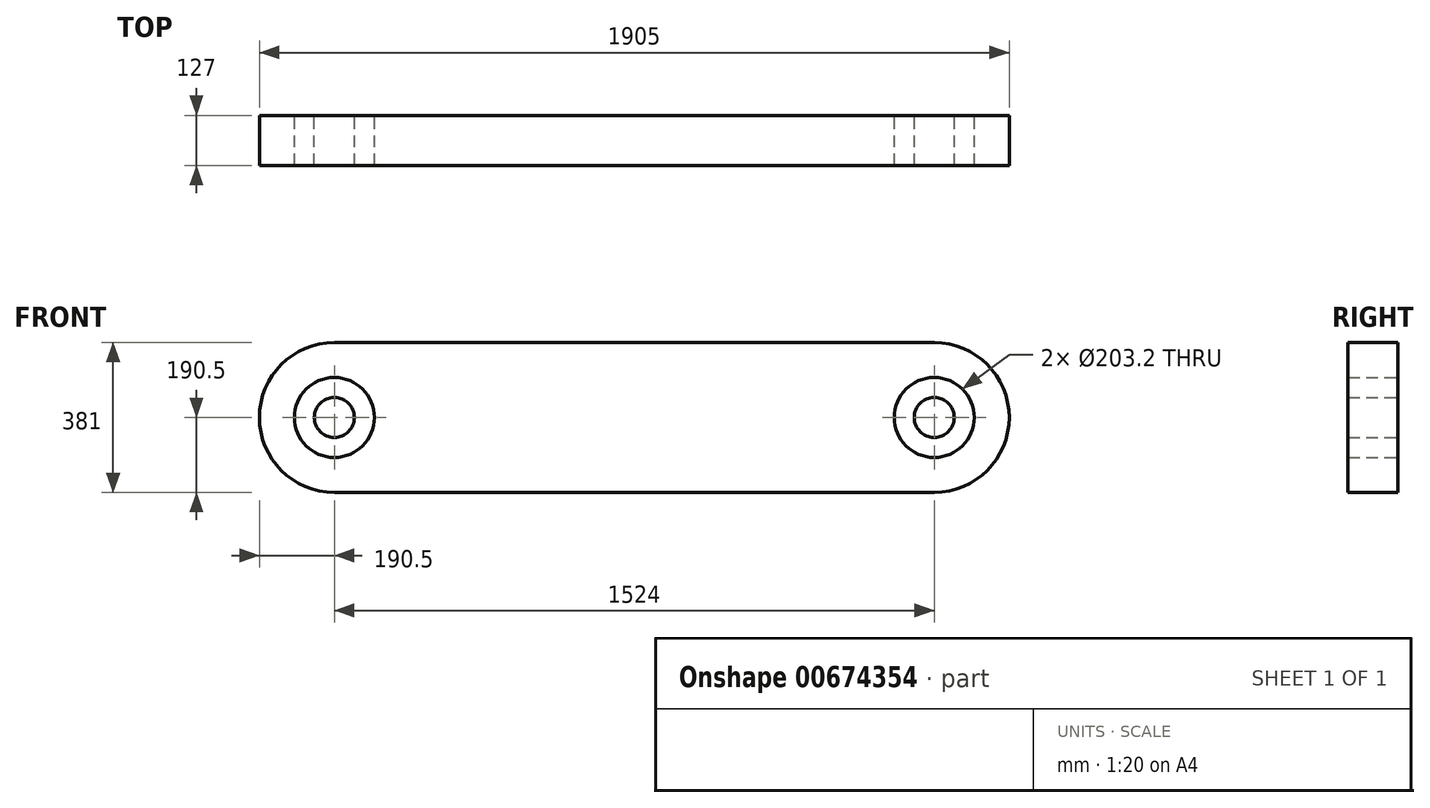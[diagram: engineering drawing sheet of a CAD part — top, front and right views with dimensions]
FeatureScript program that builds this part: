
annotation { "Feature Type Name" : "Feature", "Feature Type Description" : "" }
export const myFeature = defineFeature(function(context is Context, id is Id, definition is map)
    precondition{}
    {
        {
            var Q0;
            Q0=qCreatedBy(makeId("Front.planeOp"),FACE);
            var sketch = newSketch(context, id + "F0", { "sketchPlane" : qUnion([Q0])});
            skLineSegment(sketch, "E0.bottom", {"start": v(0, 0) * mm, "end": v(1524, 0) * mm});
            skLineSegment(sketch, "E0.top", {"start": v(0, 381) * mm, "end": v(1524, 381) * mm});
            skArc(sketch, "E1", {"start": v(0, 381) * mm, "mid": v(-190.5, 190.5) * mm, "end": v(0, 0) * mm});
            skArc(sketch, "E2", {"start": v(1524, 0) * mm, "mid": v(1714.5, 190.5) * mm, "end": v(1524, 381) * mm});
            skCircle(sketch, "E3", {"center": v(0, 190.5) * mm, "radius": 101.6 * mm});
            skCircle(sketch, "E4", {"center": v(1524, 190.5) * mm, "radius": 101.6 * mm});
            skCircle(sketch, "E5", {"center": v(1524, 190.5) * mm, "radius": 50.8 * mm});
            skCircle(sketch, "E6", {"center": v(0, 190.5) * mm, "radius": 50.8 * mm});
            skSolve(sketch);
        }
        {
            var Q0;
            Q0=makeQuery(id+"F0.imprint","IMPRINT",FACE,{"disambiguationData":[TD([[makeQuery(id+"F0.imprint","IMPRINT",EDGE,{"derivedFrom":sQuery(id+"F0.wireOp",EDGE,"E0.bottom")}),1.0]])]});
            var Q1;
            Q1=makeQuery(id+"F0.imprint","IMPRINT",FACE,{"disambiguationData":[TD([[makeQuery(id+"F0.imprint","IMPRINT",EDGE,{"derivedFrom":sQuery(id+"F0.wireOp",EDGE,"E6")}),1.0]])]});
            var Q2;
            Q2=makeQuery(id+"F0.imprint","IMPRINT",FACE,{"disambiguationData":[TD([[makeQuery(id+"F0.imprint","IMPRINT",EDGE,{"derivedFrom":sQuery(id+"F0.wireOp",EDGE,"E5")}),1.0]])]});
            extrude(context, id + "F1", {"entities" : qUnion([Q0, Q1, Q2]), "depth" : 127 * mm, "offsetDistance" : 25.4 * mm});
        }
    });
